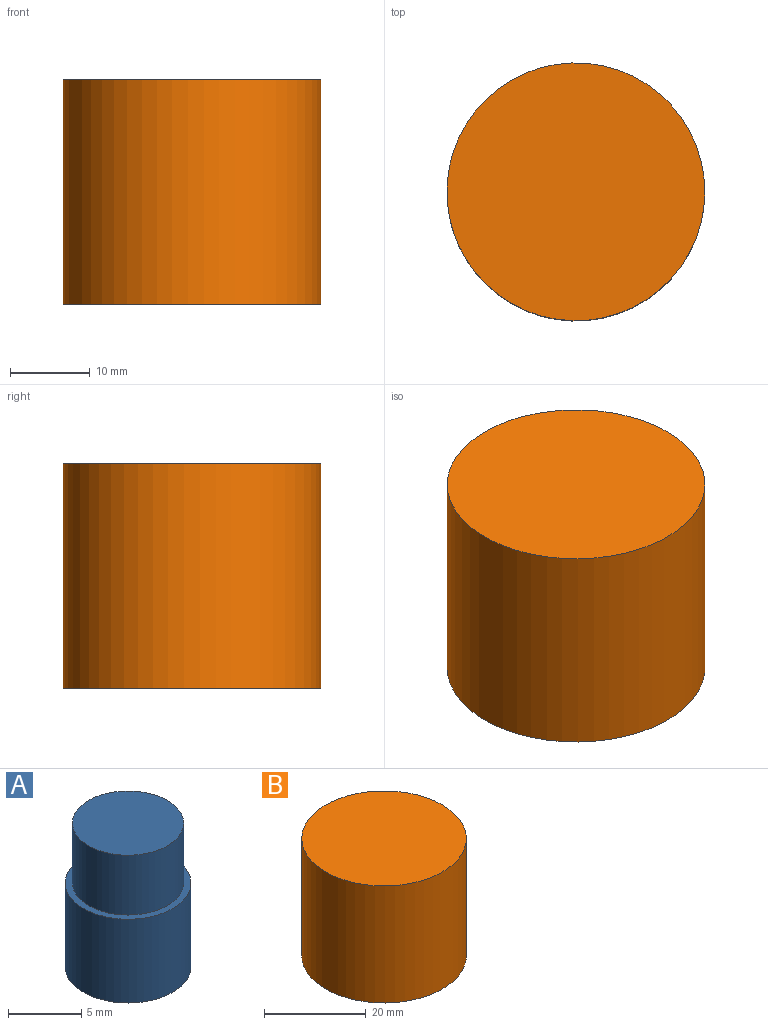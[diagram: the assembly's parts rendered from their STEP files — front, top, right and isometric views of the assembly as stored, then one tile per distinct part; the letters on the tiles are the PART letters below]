
ASSEMBLY  parts=2 mates=1
PART A: 7 faces, bbox 8.6x8.6x12 mm
  f0: plane 7.6x7.6mm, normal (0,0,1), area 45.4mm2, adj f6
  f1: plane 1x1mm, normal (0,0,-1), area 0.8mm2, adj f2
  f2: cylinder r=0.5mm len=2mm, axis (0,0,1), area 6.3mm2, adj f1,f3
  f3: plane 8.6x8.6mm, normal (0,0,-1), area 57.3mm2, adj f2,f4
  f4: cylinder r=4.3mm len=8.6mm, axis (0,0,1), area 189.1mm2, adj f3,f5
  f5: plane 8.6x8.6mm, normal (0,0,1), area 12.7mm2, adj f4,f6
  f6: cylinder r=3.8mm len=7.6mm, axis (0,0,1), area 119.4mm2, adj f0,f5
PART B: 7 faces, bbox 32.4x32.4x28.2 mm
  f0: cylinder r=4.2mm len=8.4mm, axis (0,0,1), area 131.9mm2, adj f1,f6
  f1: plane 9.4x9.4mm, normal (0,0,-1), area 14mm2, adj f0,f2
  f2: cylinder r=4.7mm len=9.4mm, axis (0,0,1), area 206.7mm2, adj f1,f3
  f3: plane 32.4x32.4mm, normal (0,0,-1), area 755.1mm2, adj f2,f4
  f4: cylinder r=16.2mm len=32.4mm, axis (0,0,1), area 2870.4mm2, adj f3,f5
  f5: plane 32.4x32.4mm, normal (0,0,1), area 824.5mm2, adj f4
  f6: sphere r=4.2mm, area 110.8mm2, adj f0
PLACE A t=(14.15,5.1,-8)mm
PLACE B t=(14.15,5.1,1.4)mm
MATE fastened B.f0 <-> A.f2  axis (0,0,-1) through (14.15,5.1,-3.6)mm
